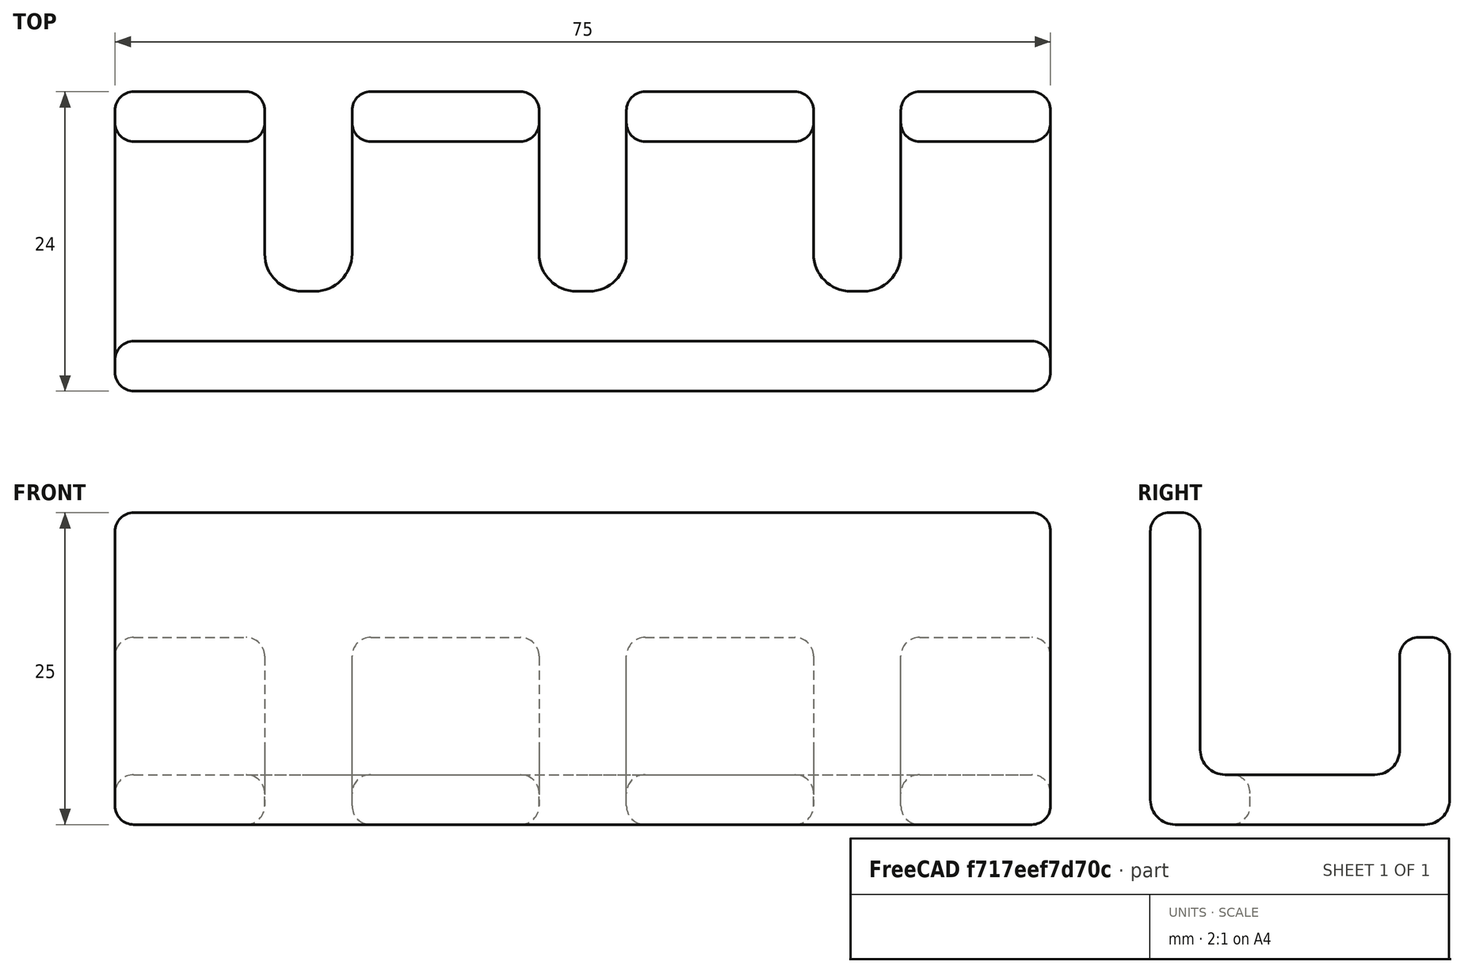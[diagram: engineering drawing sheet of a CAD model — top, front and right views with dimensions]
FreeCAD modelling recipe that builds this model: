
FCSTD DOCUMENT  (FreeCAD 0.20R29177 +426 (Git))
Label: holder2
License: All rights reserved
LicenseURL: http://en.wikipedia.org/wiki/All_rights_reserved
objects: Part::Fillet×7, Part::Box×4, Part::Feature×2, Part::MultiFuse×1, Part::Cut×1
note: 15 computed .brp shape members not serialized (recipe doc carries the construction recipe); baked Part::Feature solids carry a one-line shape summary decoded from their .brp

FEATURE [Part::Box] Box  label="Cube"
  AttacherType = Attacher::AttachEngine3D
  Height = 25
  Length = 75
  Width = 24
FEATURE [Part::Box] Box001  label="Cube001"
  AttacherType = Attacher::AttachEngine3D
  Height = 25
  Length = 75
  Placement = pos=(0,4,4) rot=(0,0,1;0rad)
  Width = 16
FEATURE [Part::Fillet] Fillet
  Base = -> Box001
  Edges = 2 edges r=2: [Edge9,Edge11]
FEATURE [Part::Fillet] Fillet001  label="Base"
  Base = -> Box
  Edges = 2 edges r=2: [Edge9,Edge11]
FEATURE [Part::Box] Box002  label="Cube002"
  AttacherType = Attacher::AttachEngine3D
  Height = 25
  Length = 7
  Placement = pos=(12,8,0) rot=(0,0,1;0rad)
  Width = 20
FEATURE [Part::Fillet] Fillet002
  Base = -> Box002
  Edges = 2 edges r=3: [Edge1,Edge5]
FEATURE [Part::Feature] Fillet002001
  Placement = pos=(19,2,0) rot=(0,0,1;0rad)
  shape: bbox 7 x 20 x 25 mm, 8 faces (baked)
FEATURE [Part::Feature] Fillet002002
  Placement = pos=(41,2,0) rot=(0,0,1;0rad)
  shape: bbox 7 x 20 x 25 mm, 8 faces (baked)
FEATURE [Part::Box] Box003  label="Cube003"
  AttacherType = Attacher::AttachEngine3D
  Height = 25
  Length = 75
  Placement = pos=(0,10,15) rot=(0,0,1;0rad)
  Width = 16
FEATURE [Part::MultiFuse] Fusion
  Shapes = -> [Fillet,Fillet002,Fillet002001,Fillet002002,Box003]
FEATURE [Part::Cut] Cut
  Base = -> Fillet001
  Tool = -> Fusion
FEATURE [Part::Fillet] Fillet002003
  Base = -> Cut
  Edges = 8 edges r=1.5: [Edge8,Edge47,Edge75,Edge86,Edge93,Edge101,Edge108,Edge116]
FEATURE [Part::Fillet] Fillet002004
  Base = -> Fillet002003
  Edges = 4 edges r=1.5: [Edge30,Edge36,Edge38,Edge42]
FEATURE [Part::Fillet] Fillet002005
  Base = -> Fillet002004
  Edges = 4 edges r=1.5: [Edge55,Edge167,Edge205,Edge218]
FEATURE [Part::Fillet] Fillet002006
  Base = -> Fillet002005
  Edges = 1 edges r=1.5: [Edge18]
